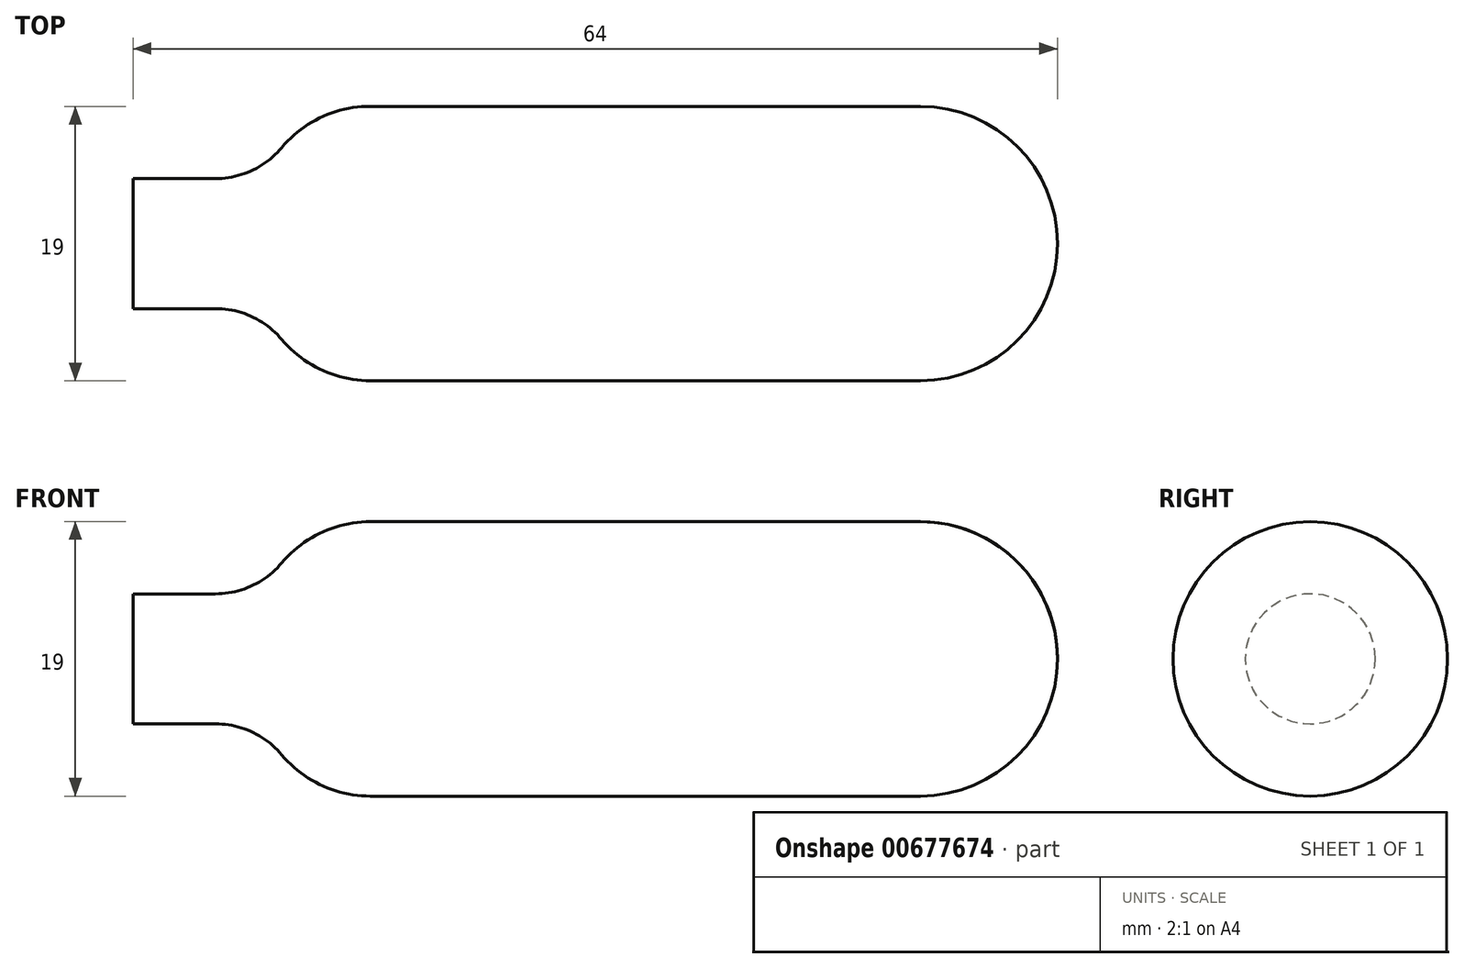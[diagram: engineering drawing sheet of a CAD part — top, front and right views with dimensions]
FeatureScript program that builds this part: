
annotation { "Feature Type Name" : "Feature", "Feature Type Description" : "" }
export const myFeature = defineFeature(function(context is Context, id is Id, definition is map)
    precondition{}
    {
        {
            var Q0;
            Q0=qCreatedBy(makeId("Front.planeOp"),FACE);
            var sketch = newSketch(context, id + "F0", { "sketchPlane" : qUnion([Q0])});
            skLineSegment(sketch, "E0", {"start": v(0, 0) * mm, "end": v(64, 0) * mm});
            skLineSegment(sketch, "E1", {"start": v(64, 0) * mm, "end": v(64, 9.5) * mm});
            skLineSegment(sketch, "E2", {"start": v(0, 0) * mm, "end": v(0, 4.5) * mm});
            skLineSegment(sketch, "E3", {"start": v(0, 4.5) * mm, "end": v(9, 4.5) * mm});
            skLineSegment(sketch, "E4", {"start": v(9, 4.5) * mm, "end": v(9, 9.5) * mm});
            skLineSegment(sketch, "E5", {"start": v(9, 9.5) * mm, "end": v(64, 9.5) * mm});
            skSolve(sketch);
        }
        {
            var Q0;
            Q0=makeQuery(id+"F0.imprint","IMPRINT",FACE,{"disambiguationData":[TD([[makeQuery(id+"F0.imprint","IMPRINT",EDGE,{"derivedFrom":sQuery(id+"F0.wireOp",EDGE,"E0")}),1.0]])]});
            var Q1;
            Q1=sQuery(id+"F0.wireOp",EDGE,"E0");
            revolve(context, id + "F1", {"entities" : qUnion([Q0]), "axis" : qUnion([Q1]), "revolveType" : RevolveType.FULL});
        }
        {
            var Q0;
            Q0=makeQuery(id+"F1.opRevolve","SWEPT_EDGE",EDGE,{"disambiguationData":[OSD([sQuery(id+"F0.wireOp",EDGE,"E4"),sQuery(id+"F0.wireOp",EDGE,"E5")])]});
            fillet(context, id + "F2", {"entities" : qUnion([Q0]), "radius" : 8 * mm, "tangentPropagation" : true, "allowEdgeOverflow" : false});
        }
        {
            var Q0;
            Q0=makeQuery(id+"F2.opFillet","BLEND_EDGE",EDGE,{"blendedFrom":[makeQuery(id+"F1.opRevolve","SWEPT_EDGE",EDGE,{"disambiguationData":[OSD([sQuery(id+"F0.wireOp",EDGE,"E4"),sQuery(id+"F0.wireOp",EDGE,"E5")])]}),makeQuery(id+"F1.opRevolve","SWEPT_FACE",FACE,{"disambiguationData":[OSD([sQuery(id+"F0.wireOp",EDGE,"E3")])]})],"blendedInto":[makeQuery(id+"F1.opRevolve","SWEPT_FACE",FACE,{"disambiguationData":[OSD([sQuery(id+"F0.wireOp",EDGE,"E3")])]})]});
            fillet(context, id + "F3", {"entities" : qUnion([Q0]), "radius" : 6 * mm, "tangentPropagation" : true, "allowEdgeOverflow" : false});
        }
        {
            var Q0;
            Q0=makeQuery(id+"F1.opRevolve","SWEPT_EDGE",EDGE,{"disambiguationData":[OSD([sQuery(id+"F0.wireOp",EDGE,"E1"),sQuery(id+"F0.wireOp",EDGE,"E5")])]});
            fillet(context, id + "F4", {"entities" : qUnion([Q0]), "radius" : 9.5 * mm, "tangentPropagation" : true, "allowEdgeOverflow" : false});
        }
    });
